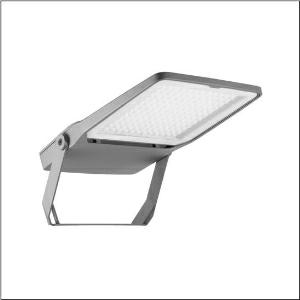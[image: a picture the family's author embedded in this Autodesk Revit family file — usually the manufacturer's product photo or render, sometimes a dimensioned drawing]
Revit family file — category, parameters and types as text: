
# Revit family: floodlight_fl_20_midi___pl52_5xa7682d1d1ac_0cf7
name_source: partatom
category: Lighting Fixtures
units: mm (PartAtom-declared; Revit-internal decimal feet)

## family parameters
Cut with Voids When Loaded = No
Host = Face
Light Source = No
Part Type = Normal
Room Calculation Point = No
Round Connector Dimension = Use Diameter
Shared = No

## types (1)
- --- (1 x LED 3000K / CRI = 80 (unbekannt), 14130 lm, 3000K)
    Apparent Load = 142 VA
    CIE Flux Codes = 27 59 98 100 100
    Color Rendering = 80
    Color Temperature = 3000K
    Default Elevation = 1800 mm
    Description = Floodlight FL 20 midi, floodlight, primary light control with lens, of plastic, primary optical cover: protective disc, of toughened safety glass, transparent, light distribution: PL52, light emission: direct distribution, primary light characteristic: asymmetric, installation type: surface-mounted, LED, High Power LED, rated luminous flux: 14.130lm, luminous efficacy: 100lm/W, light colour: 830, colour temperature: 3000K, control gear: ECG Plus, control: flexible luminous flux parameterisation, time-dependent luminous flux control, digital communication interface, power reduction, overheat protection, electronic power reduction, with terminal, 5-pole, max. 2.5mm², mains connection: 220..240V, AC, 50/60Hz, rated input power: 142W, LED unit, of diecast aluminium, powder-coated, Siteco® metallic grey (DB 702S), corrosivity category C5 mid according to DIN EN ISO 12944, incl. 1x M20 cable gland for cable Ø 6.5..12mm, length: 654mm, width: 450mm, height: 76mm, housing frame, of diecast aluminium, powder-coated, Siteco® metallic grey (DB 702S), mounting bracket, of steel, powder-coated, Siteco® metallic grey (DB 702S), DALI, protection rating (complete): IP66, insulation class (complete): insulation class II (safety insulation), certification: CE, ENEC, VDE, protection symbol: D, permissible operating ambient temperature: -40..+40°C, permissible operating ambient temperature for outdoor applications: -40..+50°C, standard: DIN EN 12944, packaging unit: 1 piece

Light Distribution: PL52
    Height = 76 mm
    Lamp = 1 x LED 3000K / CRI >= 80 (unbekannt)
    Lamp Light Flux = 14130 lm
    Lamp count = 1
    Length = 672 mm
    Luminous efficacy = 100 lm/W
    Manufacturer = Siteco
    ModVariant = No
    Model = 5XA7682D1D1AC
    Mounting Place = Wall
    Mounting Type = Surface mounted
    Number of Poles = 1
    OnlyDefault = Yes
    Power Factor = 1
    Product Name = Floodlight FL 20 midi | PL52
    Product group = floodlight | wall mounted
    ProductGroupID = 2001
    Protection Class = Protection class II
    Protection Degree = IP 66
    RLX_Detail_Level = 1
    RLX_Emergency_Light_Flux = 0 lm
    RLX_Emergency_Type = 0
    RLX_Emergency_Type_DB = No
    RlxData = <blob elided: 97745 chars, md5=df73004f>
    Socket = socket
    Standby Power = 0 W
    System Light Flux = 14130 lm
    System Power = 142 W
    Type Comments = factory setting: luminous flux: 100 % | dim-lin: 254 | 489 mA
    Type Image = l_1005943.jpg
    URL = http://relux.com
    VarID = @adj_148041
    Voltage = 0 V
    Weight = 0.00 kg
    Width = 450 mm

## geometry (parser evidence)
native form markers: Blend x4, Sweep x13
no freeform markers — native parametric forms only
